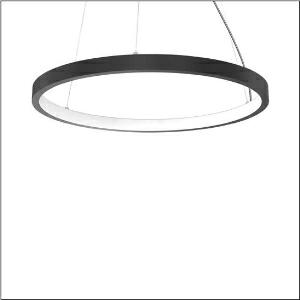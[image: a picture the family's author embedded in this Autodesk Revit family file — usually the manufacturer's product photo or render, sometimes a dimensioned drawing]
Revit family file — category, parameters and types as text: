
# Revit family: silica_21_ring-i_5pjbi4d3104a
name_source: partatom
category: Lighting Fixtures
units: mm (PartAtom-declared; Revit-internal decimal feet)

## family parameters
Cut with Voids When Loaded = No
Host = Face
Light Source = No
Part Type = Normal
Room Calculation Point = No
Round Connector Dimension = Use Diameter
Shared = No

## types (1)
- Silica 21 Ring-I (1 x LED, 8890 lm, 140 W, 4000K)
    Apparent Load = 140 VA
    CIE Flux Codes = 22 48 76 50 101
    Color Rendering = 80
    Color Temperature = 4000K
    Default Elevation = 1800 mm
    Description = Silica 21 Ring-I, suspended luminaire, of PMMA, frosted, light emission: inner ring side luminous distribution, primary light characteristic: symmetric, installation type: suspended mounting, LED, rated luminous flux: 8.890lm, luminous efficacy: 64lm/W, light colour: 840, colour temperature: 4000K, control gear: DALI 2, with terminal, 5-pole, mains connection: 230V, AC/DC, 0/50..60Hz, rated input power: 140W, housing, of extruded aluminium section, jet black (RAL 9005), diameter: 1.470mm, ceiling canopy, jet black (RAL 9005), protection rating (lamp compartment): IP40, insulation class (complete): insulation class I (protective earthing), certification: CE, impact resistance: IK02, permissible operating ambient temperature: 0..+35°C, packaging unit: 1 piece
    Height = 48 mm  [stored 0.15748 ft]
    Lamp = 1 x LED
    Lamp Light Flux = 8890 lm
    Lamp Power = 140 W
    Lamp count = 1
    Length = 1470 mm
    Luminous efficacy = 64 lm/W
    Manufacturer = Siteco
    ModVariant = No
    Model = 5PJBI4D3104A
    Mounting Place = Ceiling
    Mounting Type = Pendant
    Number of Poles = 1
    OnlyDefault = Yes
    Power Factor = 1
    Product Name = Silica 21 Ring-I
    Product group = suspended luminaire
    ProductGroupID = 904
    Protection Class = Protection class I
    Protection Degree = IP 40
    RLX_Detail_Level = 1
    RLX_Emergency_Light_Flux = 0 lm
    RLX_Emergency_Type = 0
    RLX_Emergency_Type_DB = No
    RlxData = <blob elided: 20385 chars, md5=95255455>
    Socket = socket
    Standby Power = 0 W
    System Light Flux = 8890 lm
    System Power = 140 W
    Type Comments = Product without accessories
    Type Image = l_1258373.jpg
    URL = http://relux.com
    VarID = ---
    Voltage = 0 V
    Weight = 0.00 kg
    Width = 0 mm  [stored 0 ft]

note: [stored X ft] marks values corroborated as IEEE doubles in the binary element streams (Revit-internal decimal feet)

## geometry (parser evidence)
native form markers: Blend x4, Sweep x10
no freeform markers — native parametric forms only
